# Revit family: Camera-Security-Panasonic-Super_Dynamic-Dome-Network-S2131SeriesX
name_source: partatom
category: Security Devices
revit_build: Autodesk Revit 2013 (Build: 20130531_2115(x64)
units: mm (PartAtom-declared; Revit-internal decimal feet)

## types (5) — shared parameters
Angle Of View = 110
Communication Ports = 10Base-T / 100Base-TX, RJ45 connector
Date Last Modified = 2016/10/31
Day Or Night = Yes
Diameter = 5.1 "
Equipment Abbreviation = SC
Family Version = 1.0.0
HFOV Max 169 = 110.00°
HFOV Max 43 = 90.00°
HFOV Min 169 = 30.00°
HFOV Min 43 = 25.00°
Has POE = Yes
Height = 4 "
IP Or Analog = IP
Indoor Or Outdoor = Indoor
Manufacturer = Panasonic
Model Disclaimer = Contact Panasonic for more information
Mounting Positions = Surface Mount
Operational Humidity = 10% to 90% (no condensation)
Operational Temperature = 14°F - 122°F
Pan Max = 120.00°
Pan Min = -240.00°
Panning Range = -240 to +120
Product Documentation Link = http://ssbu-t.psn-web.net
Product Material = Paint - Panasonic - Sail White
Product Page URL = http://security.panasonic.com
Provide Feedback = https://www.surveymonkey.com
Regulatory Compliance = UL UL60950-1, C-UL CAN/CSA C22.2 No.60950-1, CE, IEC60950-1 FCC Part15 ClassA, ICES003 ClassA, EN55022 ClassB, EN55024
Storage Temperature = 14°F - 122°F
Tilt Max = 85.00°
URL = http://security.panasonic.com
VFOV Max 169 = 59.00°
VFOV Max 43 = 66.00°
VFOV Min 169 = 17.00°
VFOV Min 43 = 19.00°
Vandal Resistant = No
Weight = 1.21 lb
Wide Dynamic Range = Yes
Yaw Max = 100.00°
Yaw Min = -100.00°
Yawing Range = -100 to +100
z Base Height = 2.2 "
z Base Radius = 2.5 "
z Bracket Radius = 3.7 "
z Const Pan Handle Length = 19.5 "
z Const Tilt Base Length = 9.8 "
z Const Tilt Base2 Length = 19.7 "
z Const Tilt Handle Length = 11.8 "
z Const Yaw Base Length = 10.2 "
z Const Yaw Base2 Length = 17.3 "
z Const Yaw Handle Length = 9.3 "
z Dome Material = Glass - Panasonic - Smoked
z Dome Radius = 1.8 "
z Type = 2
z VV Face Radius = 4.6 "
z VV Origin Height Offset = 0.2 "
z VV Viewpoint Depth Max = 1.2 "
z VV Viewpoint Depth Min = 0.9 "
zero-valued in all types: Default Elevation, z Zero

## per-type parameters (varying)
| type | Alarm Input Or Output Specification | Audio In | Audio Out | Description | Minimum Illumination | Part Description | Power Active | Tilt Min | Tilting Range | Voltage DC | z Camera Resolution Type |
| WV-S2131 | ALARM IN 1 (DAY/NIGHT IN, Auto time adjustment) (x1),ALARM IN 2 (ALARM OUT) (x1), ALARM IN 3 (AUX OUT) (x1) | Yes | Yes | Security Camera, Fixed Dome, Network, Super Dynamic FullHD | 0.012 lx | Security Camera, Fixed Dome, Network, Super Dynamic FullHD | 5.6 W | -30.00° | -30 to +85 | 12 V | 1 |
| WV-S2131L | ALARM IN 1 (DAY/NIGHT IN, Auto time adjustment) (x1),ALARM IN 2 (ALARM OUT) (x1), ALARM IN 3 (AUX OUT) (x1) | Yes | Yes | Security Camera, Fixed Dome, Network, Super Dynamic FullHD | 0.012 lx | Security Camera, Fixed Dome, Network, Super Dynamic FullHD | 6.8 W | -30.00° | -30 to +85 | 12 V | 1 |
| WV-S2130 | None | No | No | Security Camera, Fixed Dome, Network, Super Dynamic FullHD | 0.012 lx | Security Camera, Fixed Dome, Network, Super Dynamic FullHD | 5.3 W | -85.00° | -85 to +85 | 48 V | 1 |
| WV-S2111L | ALARM IN 1 (DAY/NIGHT IN, Auto time adjustment) (x1),ALARM IN 2 (ALARM OUT) (x1), ALARM IN 3 (AUX OUT) (x1) | Yes | Yes | Security Camera, Fixed Dome, Network, Super Dynamic HD | 0.008 lx | Security Camera, Fixed Dome, Network, Super Dynamic HD | 6.8 W | -30.00° | -30 to +85 | 12 V | 2 |
| WV-S2110 | None | No | No | Security Camera, Fixed Dome, Network, Super Dynamic HD | 0.008 lx | Security Camera, Fixed Dome, Network, Super Dynamic HD | 5.3 W | -85.00° | -85 to +85 | 48 V | 2 |

note: column(s) folded — value = type name in every type: Model, Part Number

## geometry (parser evidence)
native form markers: Extrusion x1, Sweep x5
no freeform markers — native parametric forms only
